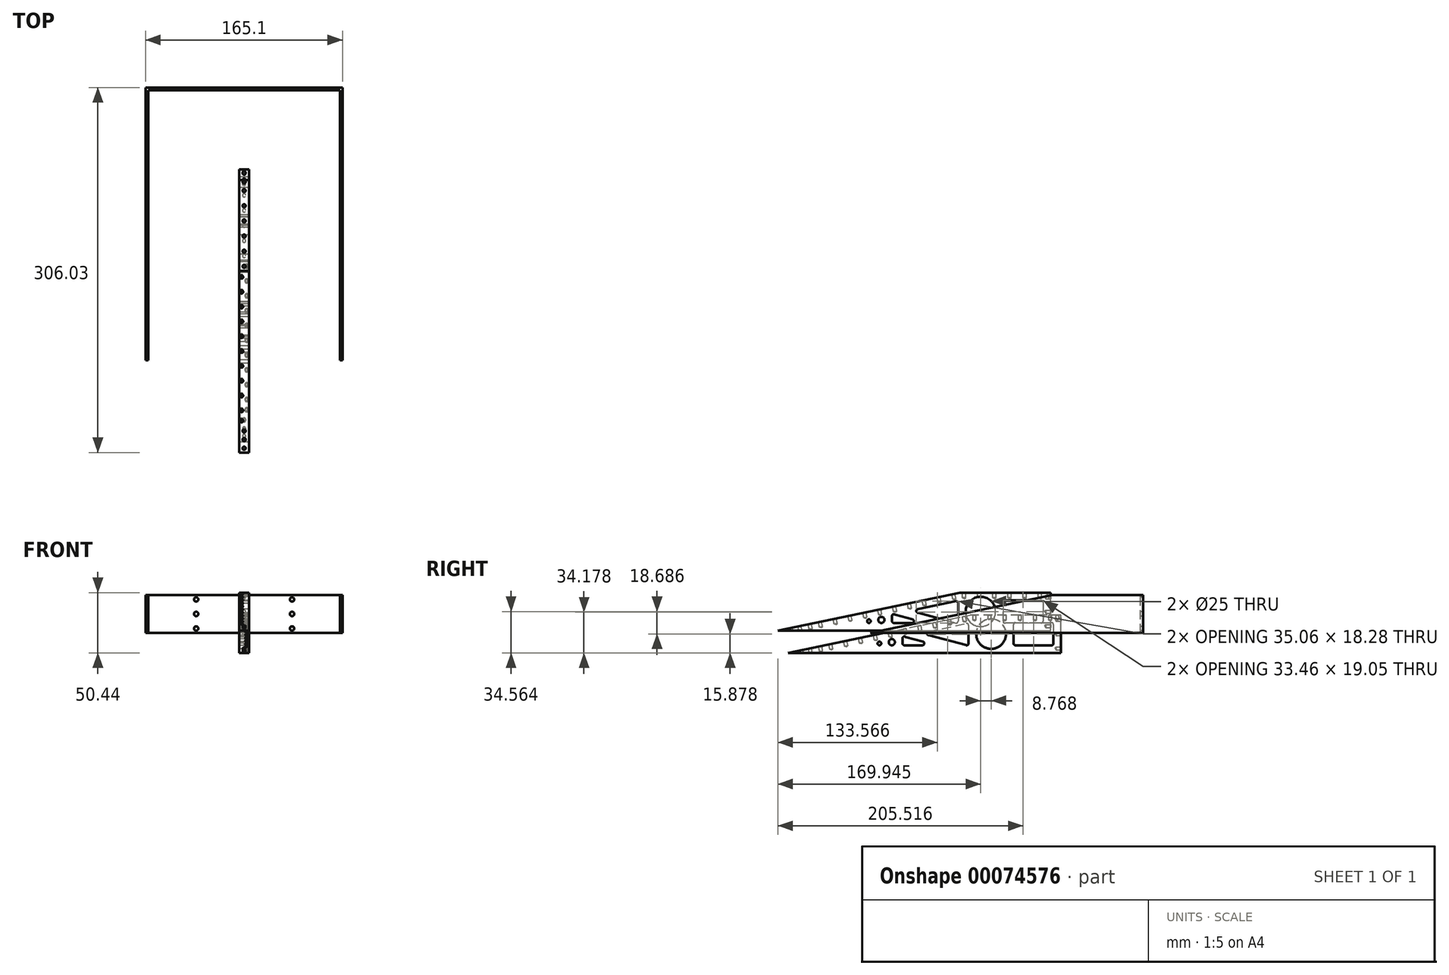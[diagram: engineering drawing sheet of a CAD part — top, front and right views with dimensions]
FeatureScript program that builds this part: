
annotation { "Feature Type Name" : "Feature", "Feature Type Description" : "" }
export const myFeature = defineFeature(function(context is Context, id is Id, definition is map)
    precondition{}
    {
        {
            var Q0;
            Q0=qCreatedBy(makeId("Right.planeOp"),FACE);
            var sketch = newSketch(context, id + "F0", { "sketchPlane" : qUnion([Q0])});
            skLineSegment(sketch, "E0", {"start": v(-101.5, 4.26) * mm, "end": v(127.1, 4.26) * mm});
            skLineSegment(sketch, "E1", {"start": v(127.1, 4.26) * mm, "end": v(127.1, 36.01) * mm});
            skLineSegment(sketch, "E2", {"start": v(127.1, 36.01) * mm, "end": v(50.9, 36.01) * mm});
            skLineSegment(sketch, "E3", {"start": v(-101.5, 4.26) * mm, "end": v(50.9, 36.01) * mm});
            skSolve(sketch);
        }
        {
            var Q0;
            Q0 = qSketchRegion(id + "F0", true);
            extrude(context, id + "F1", {"entities" : qUnion([Q0]), "endBound" : BoundingType.SYMMETRIC, "depth" : 165.1 * mm});
        }
        {
            var Q0;
            Q0=makeQuery(id+"F1.opExtrude","SWEPT_FACE",FACE,{"disambiguationData":[OSD([sQuery(id+"F0.wireOp",EDGE,"E2")])]});
            var Q1;
            Q1=makeQuery(id+"F1.opExtrude","SWEPT_FACE",FACE,{"disambiguationData":[OSD([sQuery(id+"F0.wireOp",EDGE,"E3")])]});
            var Q2;
            Q2=makeQuery(id+"F1.opExtrude","SWEPT_FACE",FACE,{"disambiguationData":[OSD([sQuery(id+"F0.wireOp",EDGE,"E0")])]});
            shell(context, id + "F2", {"entities" : qUnion([Q0, Q1, Q2]), "thickness" : 2.16 * mm});
        }
        {
            var Q0;
            Q0=qCreatedBy(makeId("Right.planeOp"),FACE);
            var sketch = newSketch(context, id + "F3", { "sketchPlane" : qUnion([Q0])});
            skLineSegment(sketch, "E4", {"start": v(-178.93, 6.22) * mm, "end": v(49.67, 6.22) * mm});
            skLineSegment(sketch, "E5", {"start": v(49.67, 6.22) * mm, "end": v(49.67, 37.97) * mm});
            skLineSegment(sketch, "E6", {"start": v(49.67, 37.97) * mm, "end": v(-26.53, 37.97) * mm});
            skLineSegment(sketch, "E7", {"start": v(-178.93, 6.22) * mm, "end": v(-26.53, 37.97) * mm});
            skPoint(sketch, "E8", {"position": v(-81.66, 18.35) * mm});
            skPoint(sketch, "E9", {"position": v(-82.1, 13.27) * mm});
            skPoint(sketch, "E10", {"position": v(-66.54, 14.16) * mm});
            skPoint(sketch, "E11", {"position": v(-61.3, 22.62) * mm});
            skPoint(sketch, "E12", {"position": v(-29.42, 14.16) * mm});
            skCircle(sketch, "E13", {"center": v(-81.66, 18.35) * mm, "radius": 1.6 * mm});
            skCircle(sketch, "E14", {"center": v(-81.66, 14.15) * mm, "radius": 1.59 * mm});
            skCircle(sketch, "E15", {"center": v(-61.3, 22.62) * mm, "radius": 1.59 * mm});
            skCircle(sketch, "E16", {"center": v(-66.54, 14.16) * mm, "radius": 1.59 * mm});
            skCircle(sketch, "E17", {"center": v(-29.42, 14.16) * mm, "radius": 1.59 * mm});
            skLineSegment(sketch, "E18", {"start": v(-83.27, 18.35) * mm, "end": v(-83.25, 14.14) * mm});
            skLineSegment(sketch, "E19", {"start": v(-81.8, 12.57) * mm, "end": v(-66.54, 12.57) * mm});
            skLineSegment(sketch, "E20", {"start": v(-80.6, 19.57) * mm, "end": v(-66.13, 15.7) * mm});
            skLineSegment(sketch, "E21", {"start": v(-62.16, 21.28) * mm, "end": v(-29.83, 12.62) * mm});
            skCircle(sketch, "E22", {"center": v(-29.42, 29.26) * mm, "radius": 1.59 * mm});
            skLineSegment(sketch, "E23", {"start": v(-61.3, 24.2) * mm, "end": v(-29.75, 30.81) * mm});
            skLineSegment(sketch, "E24", {"start": v(-27.84, 29.36) * mm, "end": v(-27.83, 14.16) * mm});
            skCircle(sketch, "E25", {"center": v(-8.99, 22.1) * mm, "radius": 12.5 * mm});
            skPoint(sketch, "E26", {"position": v(11.44, 30.03) * mm});
            skPoint(sketch, "E27", {"position": v(11.44, 14.16) * mm});
            skPoint(sketch, "E28", {"position": v(41.73, 30.03) * mm});
            skPoint(sketch, "E29", {"position": v(41.73, 14.16) * mm});
            skCircle(sketch, "E30", {"center": v(11.44, 30.03) * mm, "radius": 1.59 * mm});
            skCircle(sketch, "E31", {"center": v(11.44, 14.16) * mm, "radius": 1.59 * mm});
            skCircle(sketch, "E32", {"center": v(41.73, 30.03) * mm, "radius": 1.59 * mm});
            skCircle(sketch, "E33", {"center": v(41.73, 14.16) * mm, "radius": 1.59 * mm});
            skLineSegment(sketch, "E34", {"start": v(11.53, 31.62) * mm, "end": v(41.73, 31.62) * mm});
            skLineSegment(sketch, "E35", {"start": v(43.32, 30.04) * mm, "end": v(43.32, 14.15) * mm});
            skLineSegment(sketch, "E36", {"start": v(41.73, 12.57) * mm, "end": v(11.44, 12.57) * mm});
            skLineSegment(sketch, "E37", {"start": v(9.87, 14.39) * mm, "end": v(9.86, 30.03) * mm});
            skCircle(sketch, "E38", {"center": v(-92.2, 15.16) * mm, "radius": 2.59 * mm});
            skCircle(sketch, "E39", {"center": v(-102.6, 14.09) * mm, "radius": 1.52 * mm});
            skSolve(sketch);
        }
        {
            var Q0;
            Q0 = qSketchRegion(id + "F3", true);
            extrude(context, id + "F4", {"entities" : qUnion([Q0]), "endBound" : BoundingType.SYMMETRIC, "depth" : 8.3 * mm});
        }
        {
            var Q0;
            Q0=makeQuery(id+"F2.opShell","OFFSET_FACE",FACE,{"disambiguationData":[OSD([sQuery(id+"F0.wireOp",EDGE,"E1")])]});
            var sketch = newSketch(context, id + "F5", { "sketchPlane" : qUnion([Q0])});
            skPoint(sketch, "E40", {"position": v(-80.4, 36.01) * mm});
            skPoint(sketch, "E41", {"position": v(80.4, 36.01) * mm});
            skPoint(sketch, "E42", {"position": v(0, 36.01) * mm});
            skPoint(sketch, "E43", {"position": v(40.2, 36.01) * mm});
            skPoint(sketch, "E44", {"position": v(-40.2, 36.01) * mm});
            skPoint(sketch, "E45", {"position": v(20.96, 36.01) * mm});
            skPoint(sketch, "E46", {"position": v(20.96, 4.26) * mm});
            skCircle(sketch, "E47", {"center": v(40.2, 32.3) * mm, "radius": 1.83 * mm});
            skCircle(sketch, "E48", {"center": v(40.2, 20.14) * mm, "radius": 1.83 * mm});
            skCircle(sketch, "E49", {"center": v(40.2, 7.97) * mm, "radius": 1.83 * mm});
            skCircle(sketch, "E50", {"center": v(-40.2, 32.3) * mm, "radius": 1.83 * mm});
            skCircle(sketch, "E51", {"center": v(-40.2, 20.14) * mm, "radius": 1.83 * mm});
            skCircle(sketch, "E52", {"center": v(-40.2, 7.97) * mm, "radius": 1.83 * mm});
            skSolve(sketch);
        }
        {
            var Q0;
            Q0=makeQuery(id+"F4.opExtrude","SWEPT_FACE",FACE,{"disambiguationData":[OSD([sQuery(id+"F3.wireOp",EDGE,"E7")])]});
            var sketch = newSketch(context, id + "F6", { "sketchPlane" : qUnion([Q0])});
            skCircle(sketch, "E53", {"center": v(0, -170.2) * mm, "radius": 1.35 * mm});
            skCircle(sketch, "E54", {"center": v(0, -162.78) * mm, "radius": 1.35 * mm});
            skCircle(sketch, "E55", {"center": v(-2.08, -137.9) * mm, "radius": 1.35 * mm});
            skCircle(sketch, "E56", {"center": v(-2.08, -125.2) * mm, "radius": 1.35 * mm});
            skCircle(sketch, "E57", {"center": v(-2.08, -112.5) * mm, "radius": 1.35 * mm});
            skCircle(sketch, "E58", {"center": v(-2.08, -99.8) * mm, "radius": 1.35 * mm});
            skCircle(sketch, "E59", {"center": v(-2.08, -87.1) * mm, "radius": 1.35 * mm});
            skCircle(sketch, "E60", {"center": v(-2.08, -74.4) * mm, "radius": 1.35 * mm});
            skPoint(sketch, "E61", {"position": v(0, -18.23) * mm});
            skCircle(sketch, "E62", {"center": v(-2.08, -61.7) * mm, "radius": 1.35 * mm});
            skCircle(sketch, "E63", {"center": v(-2.08, -49) * mm, "radius": 1.35 * mm});
            skCircle(sketch, "E64", {"center": v(-2.08, -36.3) * mm, "radius": 1.35 * mm});
            skCircle(sketch, "E65", {"center": v(-2.08, -23.6) * mm, "radius": 1.35 * mm});
            skCircle(sketch, "E66", {"center": v(-2.08, -146.64) * mm, "radius": 1.35 * mm});
            skCircle(sketch, "E67", {"center": v(0, -155.36) * mm, "radius": 1.35 * mm});
            skPoint(sketch, "E68", {"position": v(-4.15, -137.71) * mm});
            skText(sketch, "E69", { "text": "drilling from narrow end back.\nall holes .106 (#36)", "fontName": "OpenSans-Regular.ttf"});
            const initialGuessF6  = {"E69": [-0.13692, -0.19265, 1, 0, 0.00771]};
            skSetInitialGuess(sketch, initialGuessF6);
            skSolve(sketch);
        }
        {
            var Q0;
            Q0=sQuery(id+"F6.wireOp",VERTEX,"E53.center");
            var Q1;
            Q1=sQuery(id+"F6.wireOp",VERTEX,"E54.center");
            var Q2;
            Q2=sQuery(id+"F6.wireOp",VERTEX,"E67.center");
            var Q3;
            Q3=sQuery(id+"F6.wireOp",VERTEX,"E66.center");
            var Q4;
            Q4=sQuery(id+"F6.wireOp",VERTEX,"E55.center");
            var Q5;
            Q5=sQuery(id+"F6.wireOp",VERTEX,"E56.center");
            var Q6;
            Q6=sQuery(id+"F6.wireOp",VERTEX,"E57.center");
            var Q7;
            Q7=sQuery(id+"F6.wireOp",VERTEX,"E58.center");
            var Q8;
            Q8=sQuery(id+"F6.wireOp",VERTEX,"E59.center");
            var Q9;
            Q9=sQuery(id+"F6.wireOp",VERTEX,"E60.center");
            var Q10;
            Q10=sQuery(id+"F6.wireOp",VERTEX,"E62.center");
            var Q11;
            Q11=sQuery(id+"F6.wireOp",VERTEX,"E63.center");
            var Q12;
            Q12=sQuery(id+"F6.wireOp",VERTEX,"E64.center");
            var Q13;
            Q13=sQuery(id+"F6.wireOp",VERTEX,"E65.center");
            var Q14;
            Q14=makeQuery(id+"F4.opExtrude","SWEPT_BODY",BODY,{"disambiguationData":[OSD([sQuery(id+"F3.wireOp",EDGE,"E4"),sQuery(id+"F3.wireOp",EDGE,"E5"),sQuery(id+"F3.wireOp",EDGE,"E6"),sQuery(id+"F3.wireOp",EDGE,"E7"),sQuery(id+"F3.wireOp",EDGE,"E13"),sQuery(id+"F3.wireOp",EDGE,"E14"),sQuery(id+"F3.wireOp",EDGE,"E15"),sQuery(id+"F3.wireOp",EDGE,"E16"),sQuery(id+"F3.wireOp",EDGE,"E17"),sQuery(id+"F3.wireOp",EDGE,"E18"),sQuery(id+"F3.wireOp",EDGE,"E19"),sQuery(id+"F3.wireOp",EDGE,"E20"),sQuery(id+"F3.wireOp",EDGE,"E21"),sQuery(id+"F3.wireOp",EDGE,"E22"),sQuery(id+"F3.wireOp",EDGE,"E23"),sQuery(id+"F3.wireOp",EDGE,"E24"),sQuery(id+"F3.wireOp",EDGE,"E25"),sQuery(id+"F3.wireOp",EDGE,"E30"),sQuery(id+"F3.wireOp",EDGE,"E31"),sQuery(id+"F3.wireOp",EDGE,"E32"),sQuery(id+"F3.wireOp",EDGE,"E33"),sQuery(id+"F3.wireOp",EDGE,"E34"),sQuery(id+"F3.wireOp",EDGE,"E35"),sQuery(id+"F3.wireOp",EDGE,"E36"),sQuery(id+"F3.wireOp",EDGE,"E37"),sQuery(id+"F3.wireOp",EDGE,"E38"),sQuery(id+"F3.wireOp",EDGE,"E39")])]});
            hole(context, id + "F7", {"style" : HoleStyle.SIMPLE, "holeDiameter" : 2.7 * mm, "endStyle" : HoleEndStyle.BLIND, "holeDepth" : 4.2 * mm, "locations" : qUnion([Q0, Q1, Q2, Q3, Q4, Q5, Q6, Q7, Q8, Q9, Q10, Q11, Q12, Q13]), "scope" : qUnion([Q14])});
        }
        {
            var Q0;
            Q0=makeQuery(id+"F4.opExtrude","SWEPT_FACE",FACE,{"disambiguationData":[OSD([sQuery(id+"F3.wireOp",EDGE,"E6")])]});
            var sketch = newSketch(context, id + "F8", { "sketchPlane" : qUnion([Q0])});
            skCircle(sketch, "E70", {"center": v(0, -22.83) * mm, "radius": 1.35 * mm});
            skCircle(sketch, "E71", {"center": v(0, -10.13) * mm, "radius": 1.35 * mm});
            skCircle(sketch, "E72", {"center": v(0, 2.57) * mm, "radius": 1.35 * mm});
            skCircle(sketch, "E73", {"center": v(0, 15.27) * mm, "radius": 1.35 * mm});
            skCircle(sketch, "E74", {"center": v(0, 27.97) * mm, "radius": 1.35 * mm});
            skCircle(sketch, "E75", {"center": v(0, 40.67) * mm, "radius": 1.35 * mm});
            skCircle(sketch, "E76", {"center": v(0, 48.07) * mm, "radius": 1.35 * mm});
            skSolve(sketch);
        }
        {
            var Q0;
            Q0=sQuery(id+"F8.wireOp",VERTEX,"E70.center");
            var Q1;
            Q1=sQuery(id+"F8.wireOp",VERTEX,"E71.center");
            var Q2;
            Q2=sQuery(id+"F8.wireOp",VERTEX,"E72.center");
            var Q3;
            Q3=sQuery(id+"F8.wireOp",VERTEX,"E73.center");
            var Q4;
            Q4=sQuery(id+"F8.wireOp",VERTEX,"E74.center");
            var Q5;
            Q5=sQuery(id+"F8.wireOp",VERTEX,"E75.center");
            var Q6;
            Q6=sQuery(id+"F8.wireOp",VERTEX,"E76.center");
            var Q7;
            Q7=makeQuery(id+"F4.opExtrude","SWEPT_BODY",BODY,{"disambiguationData":[OSD([sQuery(id+"F3.wireOp",EDGE,"E4"),sQuery(id+"F3.wireOp",EDGE,"E5"),sQuery(id+"F3.wireOp",EDGE,"E6"),sQuery(id+"F3.wireOp",EDGE,"E7"),sQuery(id+"F3.wireOp",EDGE,"E13"),sQuery(id+"F3.wireOp",EDGE,"E14"),sQuery(id+"F3.wireOp",EDGE,"E15"),sQuery(id+"F3.wireOp",EDGE,"E16"),sQuery(id+"F3.wireOp",EDGE,"E17"),sQuery(id+"F3.wireOp",EDGE,"E18"),sQuery(id+"F3.wireOp",EDGE,"E19"),sQuery(id+"F3.wireOp",EDGE,"E20"),sQuery(id+"F3.wireOp",EDGE,"E21"),sQuery(id+"F3.wireOp",EDGE,"E22"),sQuery(id+"F3.wireOp",EDGE,"E23"),sQuery(id+"F3.wireOp",EDGE,"E24"),sQuery(id+"F3.wireOp",EDGE,"E25"),sQuery(id+"F3.wireOp",EDGE,"E30"),sQuery(id+"F3.wireOp",EDGE,"E31"),sQuery(id+"F3.wireOp",EDGE,"E32"),sQuery(id+"F3.wireOp",EDGE,"E33"),sQuery(id+"F3.wireOp",EDGE,"E34"),sQuery(id+"F3.wireOp",EDGE,"E35"),sQuery(id+"F3.wireOp",EDGE,"E36"),sQuery(id+"F3.wireOp",EDGE,"E37"),sQuery(id+"F3.wireOp",EDGE,"E38"),sQuery(id+"F3.wireOp",EDGE,"E39")])]});
            hole(context, id + "F9", {"style" : HoleStyle.SIMPLE, "endStyle" : HoleEndStyle.BLIND, "holeDiameter" : 2.7 * mm, "holeDepth" : 4.2 * mm, "locations" : qUnion([Q0, Q1, Q2, Q3, Q4, Q5, Q6]), "scope" : qUnion([Q7])});
        }
        {
            var Q0;
            Q0=makeQuery(id+"F4.opExtrude","SWEPT_FACE",FACE,{"disambiguationData":[OSD([sQuery(id+"F3.wireOp",EDGE,"E5")])]});
            var sketch = newSketch(context, id + "F10", { "sketchPlane" : qUnion([Q0])});
            skCircle(sketch, "E77", {"center": v(0, 34.26) * mm, "radius": 1.35 * mm});
            skCircle(sketch, "E78", {"center": v(0, 22.1) * mm, "radius": 1.35 * mm});
            skCircle(sketch, "E79", {"center": v(0, 9.93) * mm, "radius": 1.35 * mm});
            skPoint(sketch, "E80", {"position": v(-4.15, 37.97) * mm});
            skPoint(sketch, "E81", {"position": v(4.15, 37.97) * mm});
            skPoint(sketch, "E82", {"position": v(-4.15, 6.22) * mm});
            skSolve(sketch);
        }
        {
            var Q0;
            Q0=sQuery(id+"F10.wireOp",VERTEX,"E77.center");
            var Q1;
            Q1=sQuery(id+"F10.wireOp",VERTEX,"E78.center");
            var Q2;
            Q2=sQuery(id+"F10.wireOp",VERTEX,"E79.center");
            var Q3;
            Q3=makeQuery(id+"F4.opExtrude","SWEPT_BODY",BODY,{"disambiguationData":[OSD([sQuery(id+"F3.wireOp",EDGE,"E4"),sQuery(id+"F3.wireOp",EDGE,"E5"),sQuery(id+"F3.wireOp",EDGE,"E6"),sQuery(id+"F3.wireOp",EDGE,"E7"),sQuery(id+"F3.wireOp",EDGE,"E13"),sQuery(id+"F3.wireOp",EDGE,"E14"),sQuery(id+"F3.wireOp",EDGE,"E15"),sQuery(id+"F3.wireOp",EDGE,"E16"),sQuery(id+"F3.wireOp",EDGE,"E17"),sQuery(id+"F3.wireOp",EDGE,"E18"),sQuery(id+"F3.wireOp",EDGE,"E19"),sQuery(id+"F3.wireOp",EDGE,"E20"),sQuery(id+"F3.wireOp",EDGE,"E21"),sQuery(id+"F3.wireOp",EDGE,"E22"),sQuery(id+"F3.wireOp",EDGE,"E23"),sQuery(id+"F3.wireOp",EDGE,"E24"),sQuery(id+"F3.wireOp",EDGE,"E25"),sQuery(id+"F3.wireOp",EDGE,"E30"),sQuery(id+"F3.wireOp",EDGE,"E31"),sQuery(id+"F3.wireOp",EDGE,"E32"),sQuery(id+"F3.wireOp",EDGE,"E33"),sQuery(id+"F3.wireOp",EDGE,"E34"),sQuery(id+"F3.wireOp",EDGE,"E35"),sQuery(id+"F3.wireOp",EDGE,"E36"),sQuery(id+"F3.wireOp",EDGE,"E37"),sQuery(id+"F3.wireOp",EDGE,"E38"),sQuery(id+"F3.wireOp",EDGE,"E39")])]});
            hole(context, id + "F11", {"style" : HoleStyle.SIMPLE, "endStyle" : HoleEndStyle.BLIND, "holeDiameter" : 2.7 * mm, "holeDepth" : 4.2 * mm, "locations" : qUnion([Q0, Q1, Q2]), "scope" : qUnion([Q3])});
        }
        {
            var Q0;
            Q0=qCreatedBy(makeId("Right.planeOp"),FACE);
            var sketch = newSketch(context, id + "F12", { "sketchPlane" : qUnion([Q0])});
            skLineSegment(sketch, "E83", {"start": v(-170.17, -12.47) * mm, "end": v(58.43, -12.47) * mm});
            skLineSegment(sketch, "E84", {"start": v(58.43, -12.47) * mm, "end": v(58.43, 19.28) * mm});
            skLineSegment(sketch, "E85", {"start": v(58.43, 19.28) * mm, "end": v(-17.77, 19.28) * mm});
            skLineSegment(sketch, "E86", {"start": v(-170.17, -12.47) * mm, "end": v(-17.77, 19.28) * mm});
            skPoint(sketch, "E87", {"position": v(-72.9, -0.33) * mm});
            skPoint(sketch, "E88", {"position": v(-73.33, -5.41) * mm});
            skPoint(sketch, "E89", {"position": v(-57.77, -4.53) * mm});
            skPoint(sketch, "E90", {"position": v(-52.54, 3.93) * mm});
            skPoint(sketch, "E91", {"position": v(-20.65, -4.53) * mm});
            skCircle(sketch, "E92", {"center": v(-72.9, -0.33) * mm, "radius": 1.6 * mm});
            skCircle(sketch, "E93", {"center": v(-72.9, -4.54) * mm, "radius": 1.59 * mm});
            skCircle(sketch, "E94", {"center": v(-52.54, 3.93) * mm, "radius": 1.59 * mm});
            skCircle(sketch, "E95", {"center": v(-57.77, -4.53) * mm, "radius": 1.59 * mm});
            skCircle(sketch, "E96", {"center": v(-20.65, -4.53) * mm, "radius": 1.59 * mm});
            skLineSegment(sketch, "E97", {"start": v(-74.5, -0.33) * mm, "end": v(-74.48, -4.54) * mm});
            skLineSegment(sketch, "E98", {"start": v(-73.03, -6.12) * mm, "end": v(-57.77, -6.12) * mm});
            skLineSegment(sketch, "E99", {"start": v(-71.83, 0.88) * mm, "end": v(-57.36, -3) * mm});
            skLineSegment(sketch, "E100", {"start": v(-53.4, 2.6) * mm, "end": v(-21.06, -6.06) * mm});
            skCircle(sketch, "E101", {"center": v(-20.65, 10.57) * mm, "radius": 1.59 * mm});
            skLineSegment(sketch, "E102", {"start": v(-52.54, 5.52) * mm, "end": v(-20.98, 12.13) * mm});
            skLineSegment(sketch, "E103", {"start": v(-19.07, 10.67) * mm, "end": v(-19.07, -4.53) * mm});
            skCircle(sketch, "E104", {"center": v(-0.22, 3.4) * mm, "radius": 12.5 * mm});
            skPoint(sketch, "E105", {"position": v(20.21, 11.35) * mm});
            skPoint(sketch, "E106", {"position": v(20.21, -4.53) * mm});
            skPoint(sketch, "E107", {"position": v(50.5, 11.35) * mm});
            skPoint(sketch, "E108", {"position": v(50.5, -4.53) * mm});
            skCircle(sketch, "E109", {"center": v(20.21, 11.35) * mm, "radius": 1.59 * mm});
            skCircle(sketch, "E110", {"center": v(20.21, -4.53) * mm, "radius": 1.59 * mm});
            skCircle(sketch, "E111", {"center": v(50.5, 11.35) * mm, "radius": 1.59 * mm});
            skCircle(sketch, "E112", {"center": v(50.5, -4.53) * mm, "radius": 1.59 * mm});
            skLineSegment(sketch, "E113", {"start": v(20.3, 12.93) * mm, "end": v(50.5, 12.93) * mm});
            skLineSegment(sketch, "E114", {"start": v(52.08, 11.36) * mm, "end": v(52.08, -4.54) * mm});
            skLineSegment(sketch, "E115", {"start": v(50.5, -6.12) * mm, "end": v(20.21, -6.12) * mm});
            skLineSegment(sketch, "E116", {"start": v(18.64, -4.3) * mm, "end": v(18.62, 11.34) * mm});
            skCircle(sketch, "E117", {"center": v(-83.42, -3.53) * mm, "radius": 2.59 * mm});
            skCircle(sketch, "E118", {"center": v(-93.83, -4.6) * mm, "radius": 1.52 * mm});
            skSolve(sketch);
        }
        {
            var Q0;
            Q0 = qSketchRegion(id + "F12", true);
            var Q1;
            Q1=makeQuery(id+"F12.imprint","IMPRINT",FACE,{"disambiguationData":[TD([[makeQuery(id+"F12.imprint","IMPRINT",EDGE,{"derivedFrom":sQuery(id+"F12.wireOp",EDGE,"E83")}),1.0]])]});
            extrude(context, id + "F13", {"entities" : qUnion([Q0, Q1]), "endBound" : BoundingType.SYMMETRIC, "depth" : 8.3 * mm});
        }
        {
            var Q0;
            Q0=makeQuery(id+"F13.opExtrude","SWEPT_FACE",FACE,{"disambiguationData":[OSD([sQuery(id+"F12.wireOp",EDGE,"E86")])]});
            var sketch = newSketch(context, id + "F14", { "sketchPlane" : qUnion([Q0])});
            skCircle(sketch, "E119", {"center": v(0, -164.08) * mm, "radius": 1.35 * mm});
            skCircle(sketch, "E120", {"center": v(0, -158) * mm, "radius": 1.35 * mm});
            skCircle(sketch, "E121", {"center": v(2.1, -133.12) * mm, "radius": 1.35 * mm});
            skCircle(sketch, "E122", {"center": v(2.1, -120.42) * mm, "radius": 1.35 * mm});
            skCircle(sketch, "E123", {"center": v(2.1, -107.72) * mm, "radius": 1.35 * mm});
            skCircle(sketch, "E124", {"center": v(2.1, -95.02) * mm, "radius": 1.35 * mm});
            skCircle(sketch, "E125", {"center": v(2.1, -82.32) * mm, "radius": 1.35 * mm});
            skCircle(sketch, "E126", {"center": v(2.1, -69.62) * mm, "radius": 1.35 * mm});
            skCircle(sketch, "E127", {"center": v(2.1, -56.92) * mm, "radius": 1.35 * mm});
            skCircle(sketch, "E128", {"center": v(2.1, 284.25) * mm, "radius": 1.35 * mm});
            skCircle(sketch, "E129", {"center": v(2.1, -44.22) * mm, "radius": 1.35 * mm});
            skCircle(sketch, "E130", {"center": v(2.1, -18.82) * mm, "radius": 1.35 * mm});
            skCircle(sketch, "E131", {"center": v(2.1, -141.85) * mm, "radius": 1.35 * mm});
            skCircle(sketch, "E132", {"center": v(0, -150.6) * mm, "radius": 1.35 * mm});
            skText(sketch, "E133", { "text": "drilling from narrow end back.\nall holes .106 (#36)", "fontName": "OpenSans-Regular.ttf"});
            skCircle(sketch, "E134", {"center": v(2.1, -31.52) * mm, "radius": 1.35 * mm});
            const initialGuessF14  = {"E133": [-0.13523, -0.18404, 1, 0, 0.00771]};
            skSetInitialGuess(sketch, initialGuessF14);
            skSolve(sketch);
        }
        {
            var Q0;
            Q0=sQuery(id+"F14.wireOp",VERTEX,"E119.center");
            var Q1;
            Q1=sQuery(id+"F14.wireOp",VERTEX,"E120.center");
            var Q2;
            Q2=sQuery(id+"F14.wireOp",VERTEX,"E132.center");
            var Q3;
            Q3=sQuery(id+"F14.wireOp",VERTEX,"E131.center");
            var Q4;
            Q4=sQuery(id+"F14.wireOp",VERTEX,"E121.center");
            var Q5;
            Q5=sQuery(id+"F14.wireOp",VERTEX,"E122.center");
            var Q6;
            Q6=sQuery(id+"F14.wireOp",VERTEX,"E123.center");
            var Q7;
            Q7=sQuery(id+"F14.wireOp",VERTEX,"E124.center");
            var Q8;
            Q8=sQuery(id+"F14.wireOp",VERTEX,"E125.center");
            var Q9;
            Q9=sQuery(id+"F14.wireOp",VERTEX,"E126.center");
            var Q10;
            Q10=sQuery(id+"F14.wireOp",VERTEX,"E127.center");
            var Q11;
            Q11=sQuery(id+"F14.wireOp",VERTEX,"E129.center");
            var Q12;
            Q12=sQuery(id+"F14.wireOp",VERTEX,"E134.center");
            var Q13;
            Q13=sQuery(id+"F14.wireOp",VERTEX,"E130.center");
            var Q14;
            Q14=makeQuery(id+"F13.opExtrude","SWEPT_BODY",BODY,{"disambiguationData":[OSD([sQuery(id+"F12.wireOp",EDGE,"E83"),sQuery(id+"F12.wireOp",EDGE,"E84"),sQuery(id+"F12.wireOp",EDGE,"E85"),sQuery(id+"F12.wireOp",EDGE,"E86"),sQuery(id+"F12.wireOp",EDGE,"E92"),sQuery(id+"F12.wireOp",EDGE,"E93"),sQuery(id+"F12.wireOp",EDGE,"E94"),sQuery(id+"F12.wireOp",EDGE,"E95"),sQuery(id+"F12.wireOp",EDGE,"E96"),sQuery(id+"F12.wireOp",EDGE,"E97"),sQuery(id+"F12.wireOp",EDGE,"E98"),sQuery(id+"F12.wireOp",EDGE,"E99"),sQuery(id+"F12.wireOp",EDGE,"E100"),sQuery(id+"F12.wireOp",EDGE,"E101"),sQuery(id+"F12.wireOp",EDGE,"E102"),sQuery(id+"F12.wireOp",EDGE,"E103"),sQuery(id+"F12.wireOp",EDGE,"E104"),sQuery(id+"F12.wireOp",EDGE,"E109"),sQuery(id+"F12.wireOp",EDGE,"E110"),sQuery(id+"F12.wireOp",EDGE,"E111"),sQuery(id+"F12.wireOp",EDGE,"E112"),sQuery(id+"F12.wireOp",EDGE,"E113"),sQuery(id+"F12.wireOp",EDGE,"E114"),sQuery(id+"F12.wireOp",EDGE,"E115"),sQuery(id+"F12.wireOp",EDGE,"E116"),sQuery(id+"F12.wireOp",EDGE,"E117"),sQuery(id+"F12.wireOp",EDGE,"E118")])]});
            hole(context, id + "F15", {"style" : HoleStyle.SIMPLE, "endStyle" : HoleEndStyle.BLIND, "holeDiameter" : 2.7 * mm, "holeDepth" : 4.2 * mm, "locations" : qUnion([Q0, Q1, Q2, Q3, Q4, Q5, Q6, Q7, Q8, Q9, Q10, Q11, Q12, Q13]), "scope" : qUnion([Q14])});
        }
        {
            var Q0;
            Q0=makeQuery(id+"F13.opExtrude","SWEPT_FACE",FACE,{"disambiguationData":[OSD([sQuery(id+"F12.wireOp",EDGE,"E85")])]});
            var sketch = newSketch(context, id + "F16", { "sketchPlane" : qUnion([Q0])});
            skCircle(sketch, "E135", {"center": v(0, -14.06) * mm, "radius": 1.35 * mm});
            skCircle(sketch, "E136", {"center": v(0, -1.36) * mm, "radius": 1.35 * mm});
            skCircle(sketch, "E137", {"center": v(0, 11.34) * mm, "radius": 1.35 * mm});
            skCircle(sketch, "E138", {"center": v(0, 24.04) * mm, "radius": 1.35 * mm});
            skCircle(sketch, "E139", {"center": v(0, 36.74) * mm, "radius": 1.35 * mm});
            skCircle(sketch, "E140", {"center": v(0, 49.44) * mm, "radius": 1.35 * mm});
            skCircle(sketch, "E141", {"center": v(0, 55.49) * mm, "radius": 1.35 * mm});
            skSolve(sketch);
        }
        {
            var Q0;
            Q0=sQuery(id+"F16.wireOp",VERTEX,"E141.center");
            var Q1;
            Q1=sQuery(id+"F16.wireOp",VERTEX,"E140.center");
            var Q2;
            Q2=sQuery(id+"F16.wireOp",VERTEX,"E139.center");
            var Q3;
            Q3=sQuery(id+"F16.wireOp",VERTEX,"E138.center");
            var Q4;
            Q4=sQuery(id+"F16.wireOp",VERTEX,"E137.center");
            var Q5;
            Q5=sQuery(id+"F16.wireOp",VERTEX,"E135.center");
            var Q6;
            Q6=sQuery(id+"F16.wireOp",VERTEX,"E136.center");
            var Q7;
            Q7=makeQuery(id+"F13.opExtrude","SWEPT_BODY",BODY,{"disambiguationData":[OSD([sQuery(id+"F12.wireOp",EDGE,"E83"),sQuery(id+"F12.wireOp",EDGE,"E84"),sQuery(id+"F12.wireOp",EDGE,"E85"),sQuery(id+"F12.wireOp",EDGE,"E86"),sQuery(id+"F12.wireOp",EDGE,"E92"),sQuery(id+"F12.wireOp",EDGE,"E93"),sQuery(id+"F12.wireOp",EDGE,"E94"),sQuery(id+"F12.wireOp",EDGE,"E95"),sQuery(id+"F12.wireOp",EDGE,"E96"),sQuery(id+"F12.wireOp",EDGE,"E97"),sQuery(id+"F12.wireOp",EDGE,"E98"),sQuery(id+"F12.wireOp",EDGE,"E99"),sQuery(id+"F12.wireOp",EDGE,"E100"),sQuery(id+"F12.wireOp",EDGE,"E101"),sQuery(id+"F12.wireOp",EDGE,"E102"),sQuery(id+"F12.wireOp",EDGE,"E103"),sQuery(id+"F12.wireOp",EDGE,"E104"),sQuery(id+"F12.wireOp",EDGE,"E109"),sQuery(id+"F12.wireOp",EDGE,"E110"),sQuery(id+"F12.wireOp",EDGE,"E111"),sQuery(id+"F12.wireOp",EDGE,"E112"),sQuery(id+"F12.wireOp",EDGE,"E113"),sQuery(id+"F12.wireOp",EDGE,"E114"),sQuery(id+"F12.wireOp",EDGE,"E115"),sQuery(id+"F12.wireOp",EDGE,"E116"),sQuery(id+"F12.wireOp",EDGE,"E117"),sQuery(id+"F12.wireOp",EDGE,"E118")])]});
            hole(context, id + "F17", {"style" : HoleStyle.SIMPLE, "endStyle" : HoleEndStyle.BLIND, "holeDiameter" : 2.7 * mm, "holeDepth" : 4.2 * mm, "startFromSketch" : true, "locations" : qUnion([Q0, Q1, Q2, Q3, Q4, Q5, Q6]), "scope" : qUnion([Q7])});
        }
        {
            var Q0;
            Q0=makeQuery(id+"F13.opExtrude","SWEPT_FACE",FACE,{"disambiguationData":[OSD([sQuery(id+"F12.wireOp",EDGE,"E84")])]});
            var sketch = newSketch(context, id + "F18", { "sketchPlane" : qUnion([Q0])});
            skCircle(sketch, "E142", {"center": v(0, 15.57) * mm, "radius": 1.35 * mm});
            skCircle(sketch, "E143", {"center": v(0, 3.4) * mm, "radius": 1.35 * mm});
            skCircle(sketch, "E144", {"center": v(0, -8.76) * mm, "radius": 1.35 * mm});
            skPoint(sketch, "E145", {"position": v(-4.15, 19.28) * mm});
            skPoint(sketch, "E146", {"position": v(4.15, 19.28) * mm});
            skPoint(sketch, "E147", {"position": v(4.15, -12.47) * mm});
            skSolve(sketch);
        }
        {
            var Q0;
            Q0=sQuery(id+"F18.wireOp",VERTEX,"E142.center");
            var Q1;
            Q1=sQuery(id+"F18.wireOp",VERTEX,"E143.center");
            var Q2;
            Q2=sQuery(id+"F18.wireOp",VERTEX,"E144.center");
            var Q3;
            Q3=makeQuery(id+"F13.opExtrude","SWEPT_BODY",BODY,{"disambiguationData":[OSD([sQuery(id+"F12.wireOp",EDGE,"E83"),sQuery(id+"F12.wireOp",EDGE,"E84"),sQuery(id+"F12.wireOp",EDGE,"E85"),sQuery(id+"F12.wireOp",EDGE,"E86"),sQuery(id+"F12.wireOp",EDGE,"E92"),sQuery(id+"F12.wireOp",EDGE,"E93"),sQuery(id+"F12.wireOp",EDGE,"E94"),sQuery(id+"F12.wireOp",EDGE,"E95"),sQuery(id+"F12.wireOp",EDGE,"E96"),sQuery(id+"F12.wireOp",EDGE,"E97"),sQuery(id+"F12.wireOp",EDGE,"E98"),sQuery(id+"F12.wireOp",EDGE,"E99"),sQuery(id+"F12.wireOp",EDGE,"E100"),sQuery(id+"F12.wireOp",EDGE,"E101"),sQuery(id+"F12.wireOp",EDGE,"E102"),sQuery(id+"F12.wireOp",EDGE,"E103"),sQuery(id+"F12.wireOp",EDGE,"E104"),sQuery(id+"F12.wireOp",EDGE,"E109"),sQuery(id+"F12.wireOp",EDGE,"E110"),sQuery(id+"F12.wireOp",EDGE,"E111"),sQuery(id+"F12.wireOp",EDGE,"E112"),sQuery(id+"F12.wireOp",EDGE,"E113"),sQuery(id+"F12.wireOp",EDGE,"E114"),sQuery(id+"F12.wireOp",EDGE,"E115"),sQuery(id+"F12.wireOp",EDGE,"E116"),sQuery(id+"F12.wireOp",EDGE,"E117"),sQuery(id+"F12.wireOp",EDGE,"E118")])]});
            hole(context, id + "F19", {"style" : HoleStyle.SIMPLE, "endStyle" : HoleEndStyle.BLIND, "holeDiameter" : 2.7 * mm, "holeDepth" : 4.2 * mm, "startFromSketch" : true, "locations" : qUnion([Q0, Q1, Q2]), "scope" : qUnion([Q3])});
        }
        {
            var Q0;
            Q0=sQuery(id+"F5.wireOp",VERTEX,"E47.center");
            var Q1;
            Q1=sQuery(id+"F5.wireOp",VERTEX,"E48.center");
            var Q2;
            Q2=sQuery(id+"F5.wireOp",VERTEX,"E49.center");
            var Q3;
            Q3=sQuery(id+"F5.wireOp",VERTEX,"E50.center");
            var Q4;
            Q4=sQuery(id+"F5.wireOp",VERTEX,"E51.center");
            var Q5;
            Q5=sQuery(id+"F5.wireOp",VERTEX,"E52.center");
            var Q6;
            Q6=makeQuery(id+"F1.opExtrude","SWEPT_BODY",BODY,{"disambiguationData":[OSD([sQuery(id+"F0.wireOp",EDGE,"E0"),sQuery(id+"F0.wireOp",EDGE,"E1"),sQuery(id+"F0.wireOp",EDGE,"E2"),sQuery(id+"F0.wireOp",EDGE,"E3")])]});
            hole(context, id + "F20", {"style" : HoleStyle.SIMPLE, "endStyle" : HoleEndStyle.BLIND, "holeDiameter" : 3.66 * mm, "holeDepth" : 4.2 * mm, "startFromSketch" : true, "locations" : qUnion([Q0, Q1, Q2, Q3, Q4, Q5]), "scope" : qUnion([Q6])});
        }
    });
